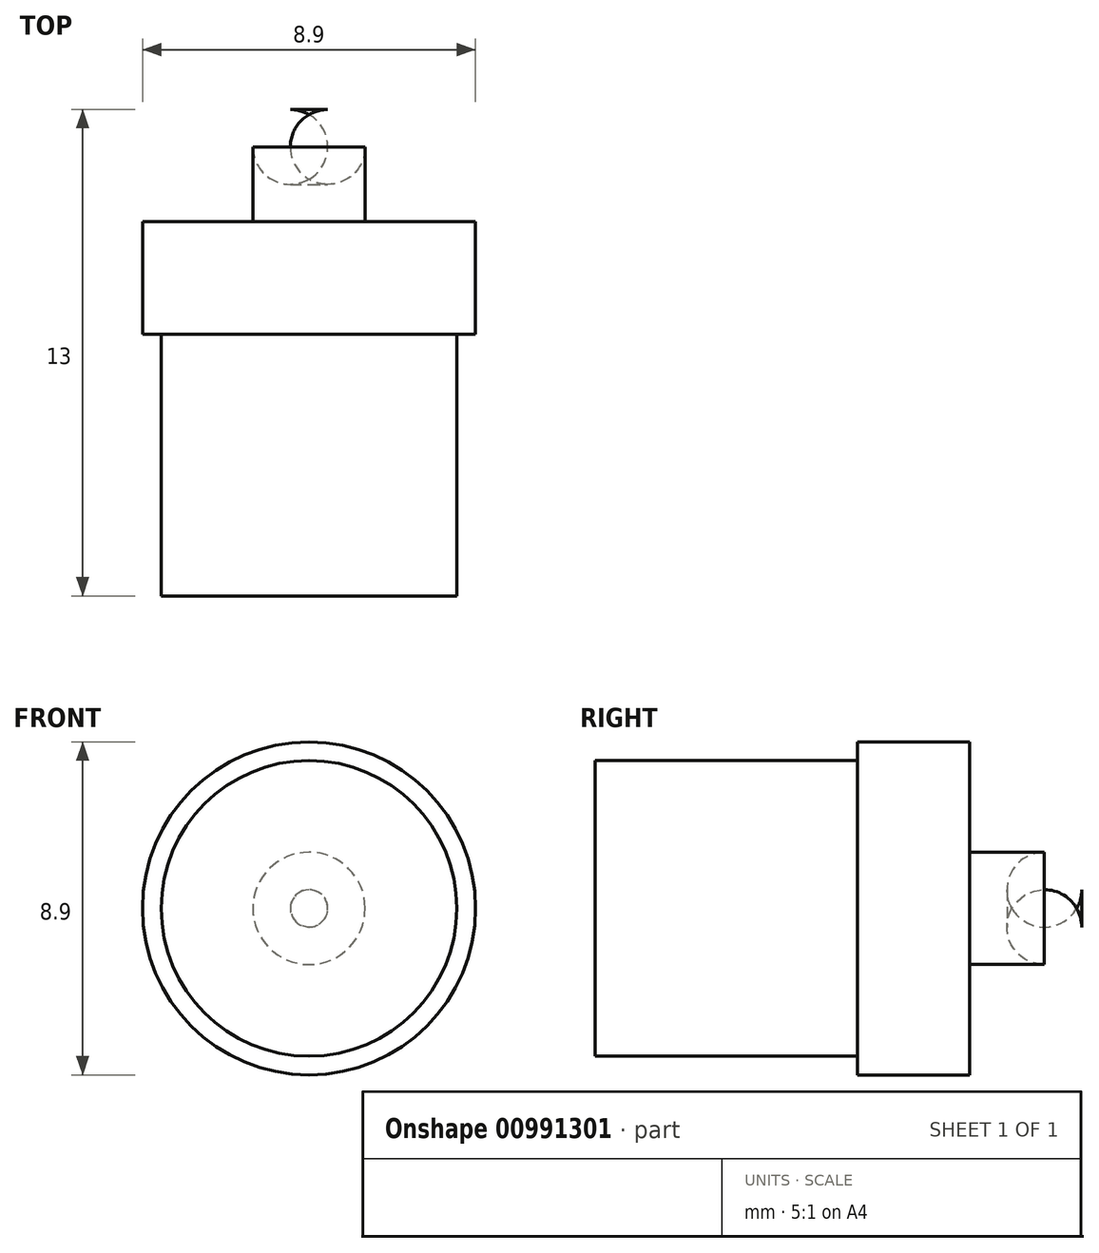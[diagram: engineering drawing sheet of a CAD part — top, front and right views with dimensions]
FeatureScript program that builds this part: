
annotation { "Feature Type Name" : "Feature", "Feature Type Description" : "" }
export const myFeature = defineFeature(function(context is Context, id is Id, definition is map)
    precondition{}
    {
        {
            var Q0;
            Q0=qCreatedBy(makeId("Right.planeOp"),FACE);
            var sketch = newSketch(context, id + "F0", { "sketchPlane" : qUnion([Q0])});
            skLineSegment(sketch, "E0", {"start": v(0, 0) * mm, "end": v(0, 1.5) * mm});
            skLineSegment(sketch, "E1", {"start": v(0, 1.5) * mm, "end": v(-3, 1.5) * mm});
            skLineSegment(sketch, "E2", {"start": v(-3, 1.5) * mm, "end": v(-3, 4.45) * mm});
            skLineSegment(sketch, "E3", {"start": v(-3, 4.45) * mm, "end": v(-6, 4.45) * mm});
            skLineSegment(sketch, "E4", {"start": v(-6, 4.45) * mm, "end": v(-6, 3.95) * mm});
            skLineSegment(sketch, "E5", {"start": v(-6, 3.95) * mm, "end": v(-13, 3.95) * mm});
            skLineSegment(sketch, "E6", {"start": v(-13, 3.95) * mm, "end": v(-13, 0) * mm});
            skLineSegment(sketch, "E7", {"start": v(-13, 0) * mm, "end": v(0, 0) * mm});
            skSolve(sketch);
        }
        {
            var Q0;
            Q0=makeQuery(id+"F0.imprint","IMPRINT",FACE,{"disambiguationData":[TD([[makeQuery(id+"F0.imprint","IMPRINT",EDGE,{"derivedFrom":sQuery(id+"F0.wireOp",EDGE,"E0")}),1.0]])]});
            var Q1;
            Q1=sQuery(id+"F0.wireOp",EDGE,"E7");
            revolve(context, id + "F1", {"surfaceOperationType" : NewSurfaceOperationType.NEW, "entities" : qUnion([Q0]), "axis" : qUnion([Q1]), "revolveType" : RevolveType.FULL});
        }
        {
            var Q0;
            Q0=makeQuery(id+"F1.opRevolve","SWEPT_EDGE",EDGE,{"disambiguationData":[OSD([sQuery(id+"F0.wireOp",EDGE,"E0"),sQuery(id+"F0.wireOp",EDGE,"E1")])]});
            fillet(context, id + "F2", {"entities" : qUnion([Q0]), "radius" : 1 * mm, "tangentPropagation" : true, "allowEdgeOverflow" : false});
        }
    });
